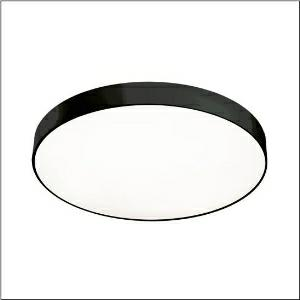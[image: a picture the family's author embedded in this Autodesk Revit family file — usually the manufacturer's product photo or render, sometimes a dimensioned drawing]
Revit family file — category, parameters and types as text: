
# Revit family: round_21_l_51mr38fd0421b
name_source: partatom
category: Lighting Fixtures
units: mm (PartAtom-declared; Revit-internal decimal feet)

## family parameters
Cut with Voids When Loaded = No
Host = Face
Light Source = No
Part Type = Normal
Room Calculation Point = No
Round Connector Dimension = Use Diameter
Shared = No

## types (1)
- Round 21 L (1 x LED, 14150 lm, 97 W, 4000K)
    Apparent Load = 97 VA
    CIE Flux Codes = 49 80 96 100 100
    Color Rendering = 80
    Color Temperature = 4000K
    Default Elevation = 1800 mm
    Description = Round 21 L, wall and ceiling luminaire, primary optical cover: cover, of PMMA, opal, light emission: direct distribution, primary light characteristic: symmetric, installation type: suspended mounting, surface-mounted, LED, rated luminous flux: 13.080lm, luminous efficacy: 146lm/W, light colour: 840, colour temperature: 4000K, control gear: DALI 2, with terminal, 5-pole, mains connection: 230V, AC, 50/60Hz, rated input power: 97W, housing, of aluminium, coated, black, diameter: 850mm, height: 62mm, protection rating (complete): IP40, insulation class (complete): insulation class I (protective earthing), certification: CE, impact resistance: IK04, permissible operating ambient temperature: -10..+35°C, packaging unit: 1 piece
    Height = 87 mm
    Lamp = 1 x LED
    Lamp Light Flux = 14150 lm
    Lamp Power = 97 W
    Lamp count = 1
    Length = 850 mm
    Luminous efficacy = 146 lm/W
    Manufacturer = Siteco
    ModVariant = No
    Model = 51MR38FD0421B
    Mounting Place = Ceiling
    Mounting Type = Surface mounted
    Number of Poles = 1
    OnlyDefault = Yes
    Power Factor = 1
    Product Name = Round 21 L
    Product group = wall and ceiling luminaire | ceiling mounted
    ProductGroupID = 304
    Protection Class = Protection class I
    Protection Degree = IP 40
    RLX_Detail_Level = 1
    RLX_Emergency_Light_Flux = 0 lm
    RLX_Emergency_Type = 0
    RLX_Emergency_Type_DB = No
    RlxData = <blob elided: 23949 chars, md5=bbde6279>
    Socket = socket
    Standby Power = 0 W
    System Light Flux = 14150 lm
    System Power = 97 W
    Type Comments = Product without accessories
    Type Image = l_1258328.jpg
    URL = http://relux.com
    VarID = ---
    Voltage = 0 V
    Weight = 0.00 kg
    Width = 0 mm  [stored 0 ft]

note: [stored X ft] marks values corroborated as IEEE doubles in the binary element streams (Revit-internal decimal feet)

## geometry (parser evidence)
native form markers: Blend x4, Sweep x10
no freeform markers — native parametric forms only
